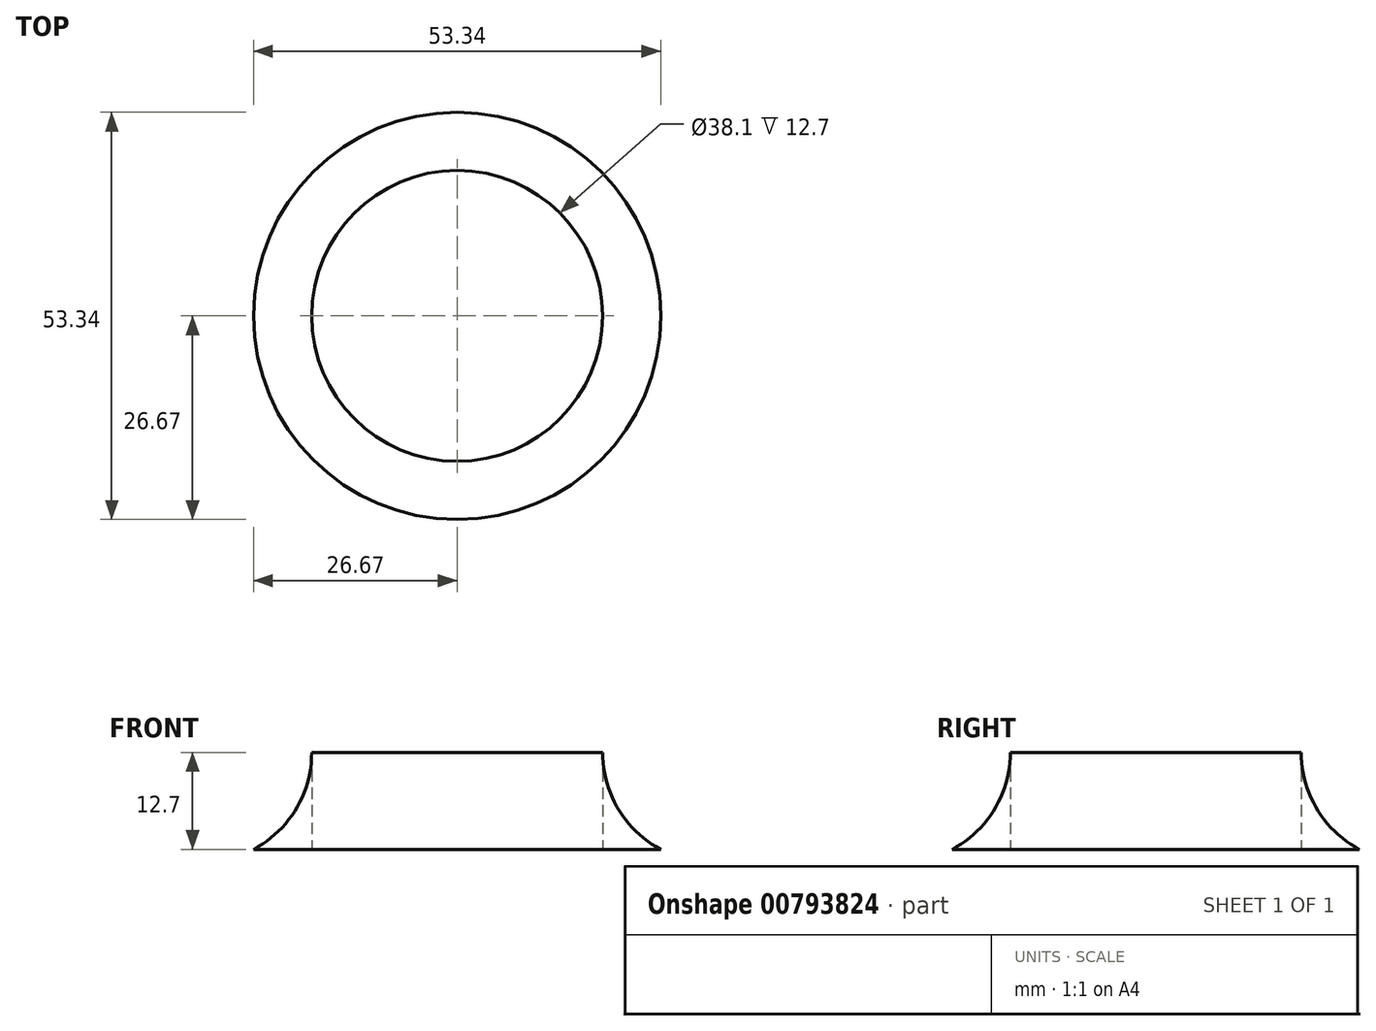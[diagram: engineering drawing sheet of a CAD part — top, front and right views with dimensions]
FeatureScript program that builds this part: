
annotation { "Feature Type Name" : "Feature", "Feature Type Description" : "" }
export const myFeature = defineFeature(function(context is Context, id is Id, definition is map)
    precondition{}
    {
        {
            var Q0;
            Q0=qCreatedBy(makeId("Front.planeOp"),FACE);
            var sketch = newSketch(context, id + "F0", { "sketchPlane" : qUnion([Q0])});
            skLineSegment(sketch, "E0", {"start": v(0, 0) * mm, "end": v(0, 12.7) * mm});
            skLineSegment(sketch, "E1", {"start": v(0, 0) * mm, "end": v(26.67, 0) * mm});
            skLineSegment(sketch, "E2", {"start": v(19.05, 0) * mm, "end": v(0, 0) * mm});
            skLineSegment(sketch, "E3", {"start": v(19.05, 0) * mm, "end": v(19.05, 12.7) * mm});
            skArc(sketch, "E4", {"start": v(19.05, 12.7) * mm, "mid": v(21.1, 5.3) * mm, "end": v(26.67, 0) * mm});
            skSolve(sketch);
        }
        {
            var Q0;
            Q0=makeQuery(id+"F0.imprint","IMPRINT",FACE,{"disambiguationData":[TD([[makeQuery(id+"F0.imprint","IMPRINT",EDGE,{"derivedFrom":sQuery(id+"F0.wireOp",EDGE,"E1")}),1.0]])]});
            var Q1;
            Q1=sQuery(id+"F0.wireOp",EDGE,"E0");
            revolve(context, id + "F1", {"surfaceOperationType" : NewSurfaceOperationType.NEW, "entities" : qUnion([Q0]), "axis" : qUnion([Q1]), "revolveType" : RevolveType.FULL});
        }
    });
